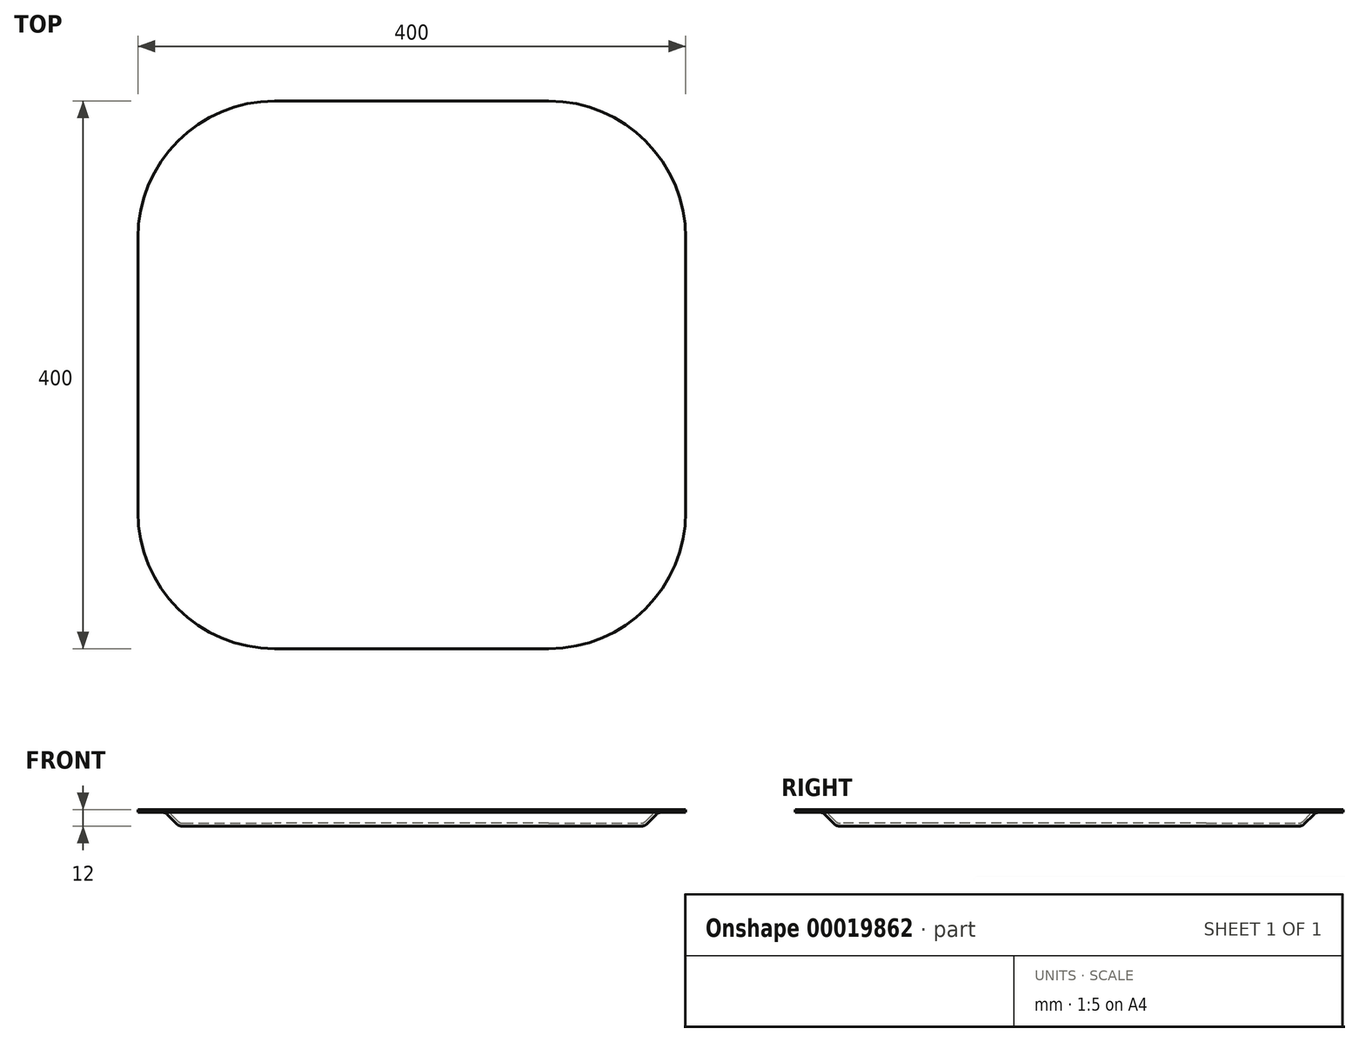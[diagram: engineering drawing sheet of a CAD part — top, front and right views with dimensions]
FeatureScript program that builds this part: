
annotation { "Feature Type Name" : "Feature", "Feature Type Description" : "" }
export const myFeature = defineFeature(function(context is Context, id is Id, definition is map)
    precondition{}
    {
        {
            var Q0;
            Q0=qCreatedBy(makeId("Top.planeOp"),FACE);
            var sketch = newSketch(context, id + "F0", { "sketchPlane" : qUnion([Q0])});
            skLineSegment(sketch, "E0.rect.bottom", {"start": v(-100, 150) * mm, "end": v(100, 150) * mm});
            skLineSegment(sketch, "E0.rect.top", {"start": v(-100, -150) * mm, "end": v(100, -150) * mm});
            skLineSegment(sketch, "E0.rect.left", {"start": v(-150, 100) * mm, "end": v(-150, -100) * mm});
            skLineSegment(sketch, "E0.rect.right", {"start": v(150, 100) * mm, "end": v(150, 0) * mm});
            skPoint(sketch, "E0.rect.middle", {"position": v(0, 0) * mm});
            skPoint(sketch, "E1.visualSharp", {"position": v(-150, 150) * mm});
            skArc(sketch, "E1.filletArc", {"start": v(-100, 150) * mm, "mid": v(-135.36, 135.36) * mm, "end": v(-150, 100) * mm});
            skPoint(sketch, "E2.visualSharp", {"position": v(150, 150) * mm});
            skArc(sketch, "E2.filletArc", {"start": v(150, 100) * mm, "mid": v(135.36, 135.36) * mm, "end": v(100, 150) * mm});
            skPoint(sketch, "E3.visualSharp", {"position": v(150, -150) * mm});
            skArc(sketch, "E3.filletArc", {"start": v(100, -150) * mm, "mid": v(135.36, -135.36) * mm, "end": v(150, -100) * mm});
            skPoint(sketch, "E4.visualSharp", {"position": v(-150, -150) * mm});
            skArc(sketch, "E4.filletArc", {"start": v(-150, -100) * mm, "mid": v(-135.36, -135.36) * mm, "end": v(-100, -150) * mm});
            skLineSegment(sketch, "E5", {"start": v(150, 0) * mm, "end": v(150, -100) * mm});
            skSolve(sketch);
        }
        {
            var Q0;
            Q0=qCreatedBy(makeId("Front.planeOp"),FACE);
            var sketch = newSketch(context, id + "F1", { "sketchPlane" : qUnion([Q0])});
            skLineSegment(sketch, "E6", {"start": v(150, 0) * mm, "end": v(170, 0) * mm});
            skLineSegment(sketch, "E7", {"start": v(170, 0) * mm, "end": v(180, 10) * mm});
            skLineSegment(sketch, "E8", {"start": v(180, 10) * mm, "end": v(200, 10) * mm});
            skLineSegment(sketch, "E9.0", {"start": v(179.17, 12) * mm, "end": v(200, 12) * mm});
            skLineSegment(sketch, "E9.1", {"start": v(169.17, 2) * mm, "end": v(179.17, 12) * mm});
            skLineSegment(sketch, "E9.2", {"start": v(150, 2) * mm, "end": v(169.17, 2) * mm});
            skLineSegment(sketch, "E10", {"start": v(150, 2) * mm, "end": v(150, 0) * mm});
            skLineSegment(sketch, "E11", {"start": v(200, 12) * mm, "end": v(200, 10) * mm});
            skSolve(sketch);
        }
        {
            var Q0;
            Q0 = qSketchRegion(id + "F1", true);
            var Q1;
            Q1=sQuery(id+"F0.wireOp",EDGE,"E0.rect.right");
            var Q2;
            Q2=sQuery(id+"F0.wireOp",EDGE,"E2.filletArc");
            var Q3;
            Q3=sQuery(id+"F0.wireOp",EDGE,"E0.rect.bottom");
            var Q4;
            Q4=sQuery(id+"F0.wireOp",EDGE,"E1.filletArc");
            var Q5;
            Q5=sQuery(id+"F0.wireOp",EDGE,"E0.rect.left");
            var Q6;
            Q6=sQuery(id+"F0.wireOp",EDGE,"E4.filletArc");
            var Q7;
            Q7=sQuery(id+"F0.wireOp",EDGE,"E0.rect.top");
            var Q8;
            Q8=sQuery(id+"F0.wireOp",EDGE,"E3.filletArc");
            var Q9;
            Q9=sQuery(id+"F0.wireOp",EDGE,"E5");
            sweep(context, id + "F2", {"profiles" : qUnion([Q0]), "path" : qUnion([Q1, Q2, Q3, Q4, Q5, Q6, Q7, Q8, Q9])});
        }
        {
            var Q0;
            Q0 = qSketchRegion(id + "F0", true);
            extrude(context, id + "F3", {"entities" : qUnion([Q0]), "operationType" : NewBodyOperationType.ADD, "depth" : 2 * mm});
        }
        {
            var Q0;
            Q0=makeQuery(id+"F2.opSweep","SWEPT_EDGE",EDGE,{"disambiguationData":[OSD([sQuery(id+"F0.wireOp",EDGE,"E0.rect.top"),sQuery(id+"F1.wireOp",EDGE,"E9.0"),sQuery(id+"F1.wireOp",EDGE,"E9.1")])]});
            fillet(context, id + "F4", {"entities" : qUnion([Q0]), "radius" : 2 * mm, "tangentPropagation" : true, "allowEdgeOverflow" : false});
        }
        {
            var Q0;
            Q0=makeQuery(id+"F2.opSweep","SWEPT_EDGE",EDGE,{"disambiguationData":[OSD([sQuery(id+"F0.wireOp",EDGE,"E4.filletArc"),sQuery(id+"F1.wireOp",EDGE,"E9.1"),sQuery(id+"F1.wireOp",EDGE,"E9.2")])]});
            var Q1;
            Q1=makeQuery(id+"F2.opSweep","SWEPT_EDGE",EDGE,{"disambiguationData":[OSD([sQuery(id+"F0.wireOp",EDGE,"E0.rect.bottom"),sQuery(id+"F1.wireOp",EDGE,"E6"),sQuery(id+"F1.wireOp",EDGE,"E7")])]});
            var Q2;
            Q2=makeQuery(id+"F2.opSweep","SWEPT_EDGE",EDGE,{"disambiguationData":[OSD([sQuery(id+"F0.wireOp",EDGE,"E0.rect.bottom"),sQuery(id+"F1.wireOp",EDGE,"E7"),sQuery(id+"F1.wireOp",EDGE,"E8")])]});
            fillet(context, id + "F5", {"entities" : qUnion([Q0, Q1, Q2]), "radius" : 5 * mm, "tangentPropagation" : true, "allowEdgeOverflow" : false});
        }
    });
